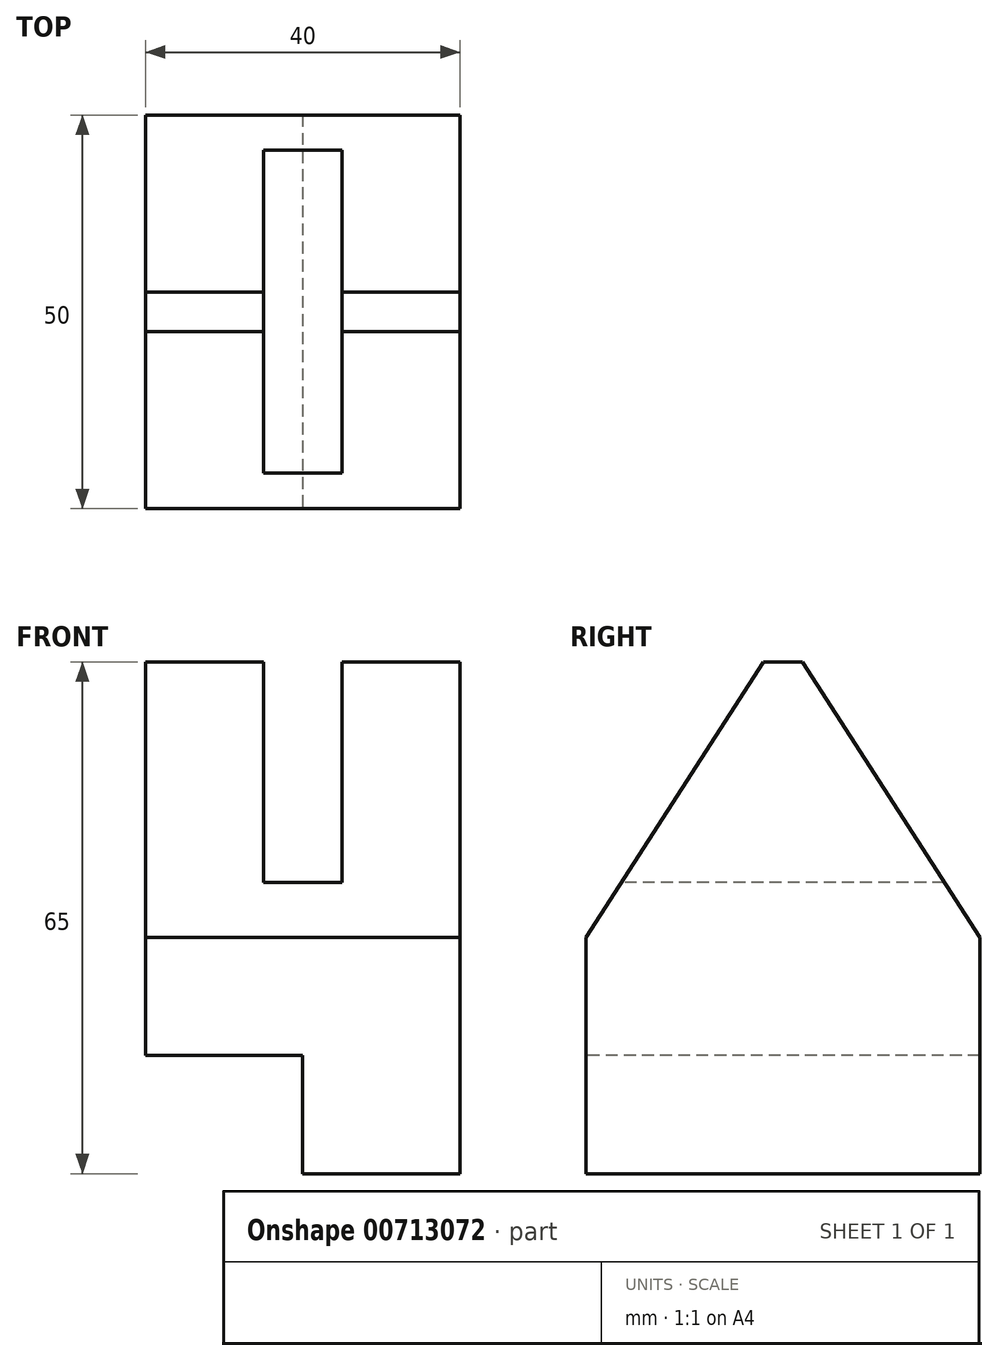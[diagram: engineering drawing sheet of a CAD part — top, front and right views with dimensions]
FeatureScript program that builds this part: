
annotation { "Feature Type Name" : "Feature", "Feature Type Description" : "" }
export const myFeature = defineFeature(function(context is Context, id is Id, definition is map)
    precondition{}
    {
        {
            var Q0;
            Q0=qCreatedBy(makeId("Right.planeOp"),FACE);
            var sketch = newSketch(context, id + "F0", { "sketchPlane" : qUnion([Q0])});
            skLineSegment(sketch, "E0.bottom", {"start": v(25, 15) * mm, "end": v(-25, 15) * mm});
            skLineSegment(sketch, "E0.top", {"start": v(25, -15) * mm, "end": v(-25, -15) * mm});
            skLineSegment(sketch, "E0.left", {"start": v(25, 15) * mm, "end": v(25, -15) * mm});
            skLineSegment(sketch, "E0.right", {"start": v(-25, 15) * mm, "end": v(-25, -15) * mm});
            skPoint(sketch, "E0.middle", {"position": v(0, 0) * mm});
            skLineSegment(sketch, "E1", {"start": v(0, 15) * mm, "end": v(0, 50) * mm});
            skLineSegment(sketch, "E2", {"start": v(0, 50) * mm, "end": v(-2.5, 50) * mm});
            skLineSegment(sketch, "E3", {"start": v(-2.5, 50) * mm, "end": v(2.5, 50) * mm});
            skLineSegment(sketch, "E4", {"start": v(2.5, 50) * mm, "end": v(25, 15) * mm});
            skLineSegment(sketch, "E5", {"start": v(-2.5, 50) * mm, "end": v(-25, 15) * mm});
            skSolve(sketch);
        }
        {
            var Q0;
            {var subQ2=sQuery(id+"F0.wireOp",EDGE,"E1");Q0=makeQuery(id+"F0.imprint","IMPRINT",FACE,{"disambiguationData":[TD([[makeQuery(id+"F0.imprint","IMPRINT",EDGE,{"derivedFrom":subQ2}),1.0]])]});}
            var Q1;
            Q1=makeQuery(id+"F0.imprint","IMPRINT",FACE,{"disambiguationData":[TD([[makeQuery(id+"F0.imprint","IMPRINT",EDGE,{"derivedFrom":sQuery(id+"F0.wireOp",EDGE,"E0.top")}),-1.0]])]});
            var Q2;
            {var subQ2=sQuery(id+"F0.wireOp",EDGE,"E1");Q2=makeQuery(id+"F0.imprint","IMPRINT",FACE,{"disambiguationData":[TD([[makeQuery(id+"F0.imprint","IMPRINT",EDGE,{"derivedFrom":subQ2}),-1.0]])]});}
            extrude(context, id + "F1", {"entities" : qUnion([Q0, Q1, Q2]), "endBound" : BoundingType.SYMMETRIC, "depth" : 40 * mm, "offsetDistance" : 25 * mm});
        }
        {
            var Q0;
            Q0=makeQuery(id+"F1.opExtrude","SWEPT_FACE",FACE,{"disambiguationData":[OSD([sQuery(id+"F0.wireOp",EDGE,"E0.right")])]});
            var sketch = newSketch(context, id + "F2", { "sketchPlane" : qUnion([Q0])});
            skLineSegment(sketch, "E6.bottom", {"start": v(-20, -15) * mm, "end": v(0, -15) * mm});
            skLineSegment(sketch, "E6.top", {"start": v(-20, 0) * mm, "end": v(0, 0) * mm});
            skLineSegment(sketch, "E6.left", {"start": v(-20, -15) * mm, "end": v(-20, 0) * mm});
            skLineSegment(sketch, "E6.right", {"start": v(0, -15) * mm, "end": v(0, 0) * mm});
            skSolve(sketch);
        }
        {
            var Q0;
            Q0=makeQuery(id+"F2.imprint","IMPRINT",FACE,{"disambiguationData":[TD([[makeQuery(id+"F2.imprint","IMPRINT",EDGE,{"derivedFrom":sQuery(id+"F2.wireOp",EDGE,"E6.bottom")}),-1.0]])]});
            extrude(context, id + "F3", {"entities" : qUnion([Q0]), "operationType" : NewBodyOperationType.REMOVE, "endBound" : BoundingType.THROUGH_ALL, "oppositeDirection" : true, "depth" : 25 * mm, "offsetDistance" : 25 * mm});
        }
        {
            var Q0;
            Q0=makeQuery(id+"F1.opExtrude","SWEPT_FACE",FACE,{"disambiguationData":[OSD([sQuery(id+"F0.wireOp",EDGE,"E3")])]});
            var sketch = newSketch(context, id + "F4", { "sketchPlane" : qUnion([Q0])});
            skLineSegment(sketch, "E7.bottom", {"start": v(5, 25) * mm, "end": v(-5, 25) * mm});
            skLineSegment(sketch, "E7.top", {"start": v(5, -25) * mm, "end": v(-5, -25) * mm});
            skLineSegment(sketch, "E7.left", {"start": v(5, 25) * mm, "end": v(5, -25) * mm});
            skLineSegment(sketch, "E7.right", {"start": v(-5, 25) * mm, "end": v(-5, -25) * mm});
            skPoint(sketch, "E7.middle", {"position": v(0, 0) * mm});
            skSolve(sketch);
        }
        {
            var Q0;
            {var subQ0=sQuery(id+"F4.wireOp",EDGE,"E7.top");Q0=makeQuery(id+"F4.imprint","IMPRINT",FACE,{"disambiguationData":[TD([[makeQuery(id+"F4.imprint","IMPRINT",EDGE,{"derivedFrom":subQ0}),-1.0]])]});}
            var Q1;
            {var subQ0=sQuery(id+"F4.wireOp",EDGE,"E7.left");var subQ1=sQuery(id+"F0.wireOp",EDGE,"E3");var subQ2=makeQuery(id+"F1.opExtrude","SWEPT_EDGE",EDGE,{"disambiguationData":[OSD([subQ1,sQuery(id+"F0.wireOp",EDGE,"E4")])]});var subQ3=makeQuery(id+"F4.imprint","INTERSECT",VERTEX,{"derivedFrom":[subQ2,subQ0]});Q1=makeQuery(id+"F4.imprint","IMPRINT",FACE,{"disambiguationData":[TD([[makeQuery(id+"F4.imprint","IMPRINT",EDGE,{"disambiguationData":[TD([[subQ3,-1.0]])],"derivedFrom":subQ0}),-1.0]])]});}
            var Q2;
            {var subQ0=sQuery(id+"F4.wireOp",EDGE,"E7.bottom");Q2=makeQuery(id+"F4.imprint","IMPRINT",FACE,{"disambiguationData":[TD([[makeQuery(id+"F4.imprint","IMPRINT",EDGE,{"derivedFrom":subQ0}),1.0]])]});}
            extrude(context, id + "F5", {"entities" : qUnion([Q0, Q1, Q2]), "operationType" : NewBodyOperationType.REMOVE, "oppositeDirection" : true, "depth" : 28 * mm, "offsetDistance" : 25 * mm});
        }
    });
